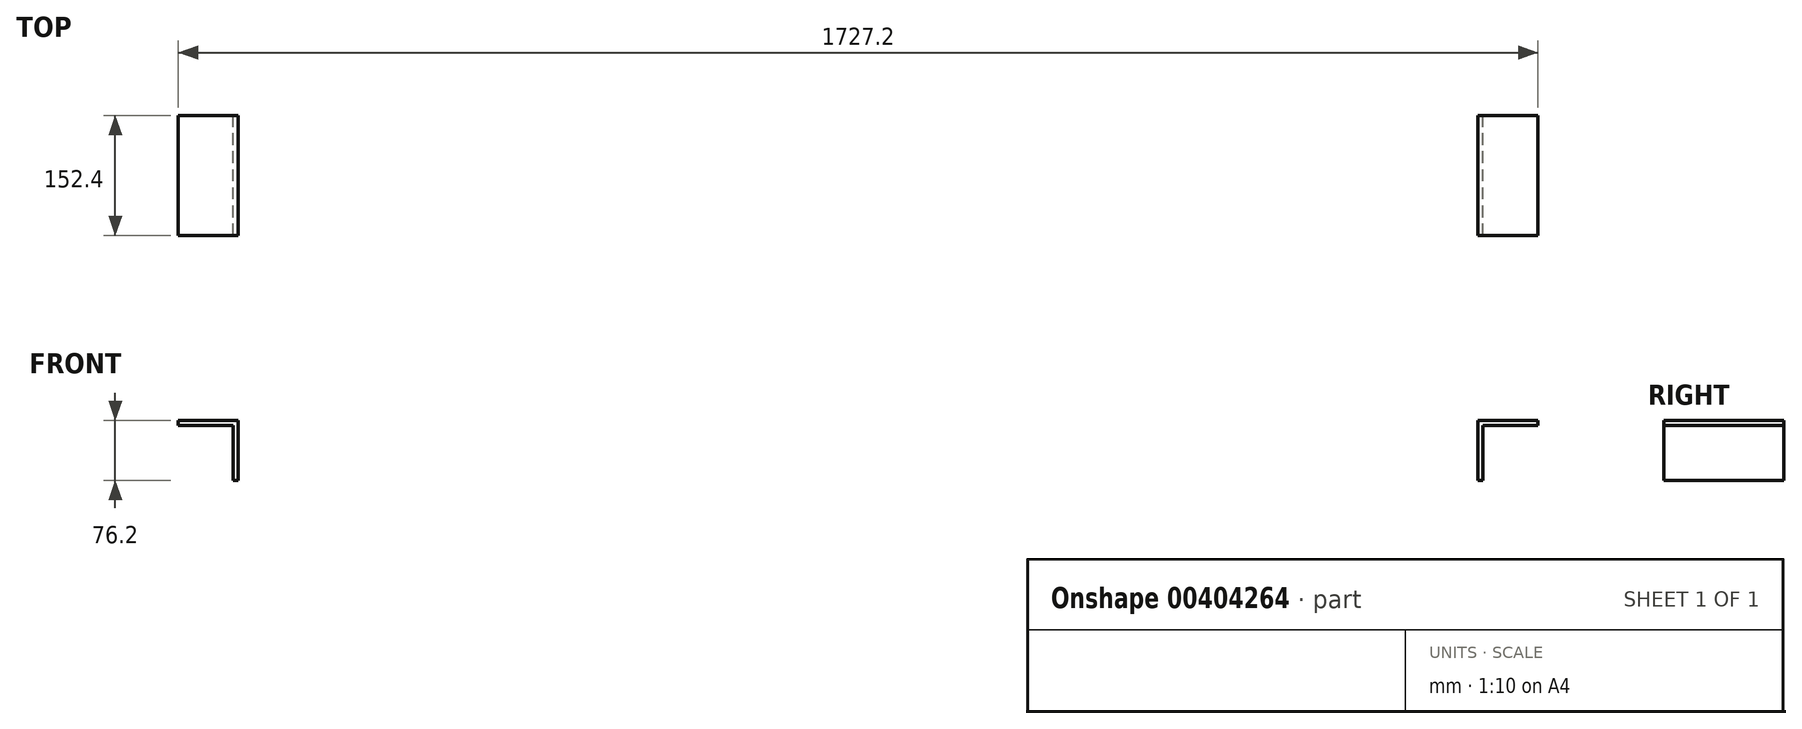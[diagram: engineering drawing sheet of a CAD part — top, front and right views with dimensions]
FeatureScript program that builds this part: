
annotation { "Feature Type Name" : "Feature", "Feature Type Description" : "" }
export const myFeature = defineFeature(function(context is Context, id is Id, definition is map)
    precondition{}
    {
        {
            var Q0;
            Q0=qCreatedBy(makeId("Front.planeOp"),FACE);
            var sketch = newSketch(context, id + "F0", { "sketchPlane" : qUnion([Q0])});
            skLineSegment(sketch, "E0", {"start": v(-863.6, 0) * mm, "end": v(-787.4, 0) * mm});
            skLineSegment(sketch, "E1", {"start": v(-787.4, 0) * mm, "end": v(-787.4, -76.2) * mm});
            skLineSegment(sketch, "E2.0", {"start": v(-863.6, -6.35) * mm, "end": v(-793.75, -6.35) * mm});
            skLineSegment(sketch, "E3.0", {"start": v(-793.75, -6.35) * mm, "end": v(-793.75, -76.2) * mm});
            skLineSegment(sketch, "E4", {"start": v(-863.6, 0) * mm, "end": v(-863.6, -6.35) * mm});
            skLineSegment(sketch, "E5", {"start": v(-793.75, -76.2) * mm, "end": v(-787.4, -76.2) * mm});
            skLineSegment(sketch, "E6.MirrorCS", {"start": v(793.75, -76.2) * mm, "end": v(787.4, -76.2) * mm});
            skLineSegment(sketch, "E7.MirrorCS", {"start": v(863.6, 0) * mm, "end": v(863.6, -6.35) * mm});
            skLineSegment(sketch, "E8.MirrorCS", {"start": v(863.6, 0) * mm, "end": v(787.4, 0) * mm});
            skLineSegment(sketch, "E9.MirrorCS", {"start": v(787.4, 0) * mm, "end": v(787.4, -76.2) * mm});
            skLineSegment(sketch, "E10.MirrorCS", {"start": v(863.6, -6.35) * mm, "end": v(793.75, -6.35) * mm});
            skLineSegment(sketch, "E11.MirrorCS", {"start": v(793.75, -6.35) * mm, "end": v(793.75, -76.2) * mm});
            skSolve(sketch);
        }
        {
            var Q0;
            Q0 = qSketchRegion(id + "F0", true);
            extrude(context, id + "F1", {"entities" : qUnion([Q0]), "endBound" : BoundingType.SYMMETRIC, "depth" : 152.4 * mm});
        }
    });
